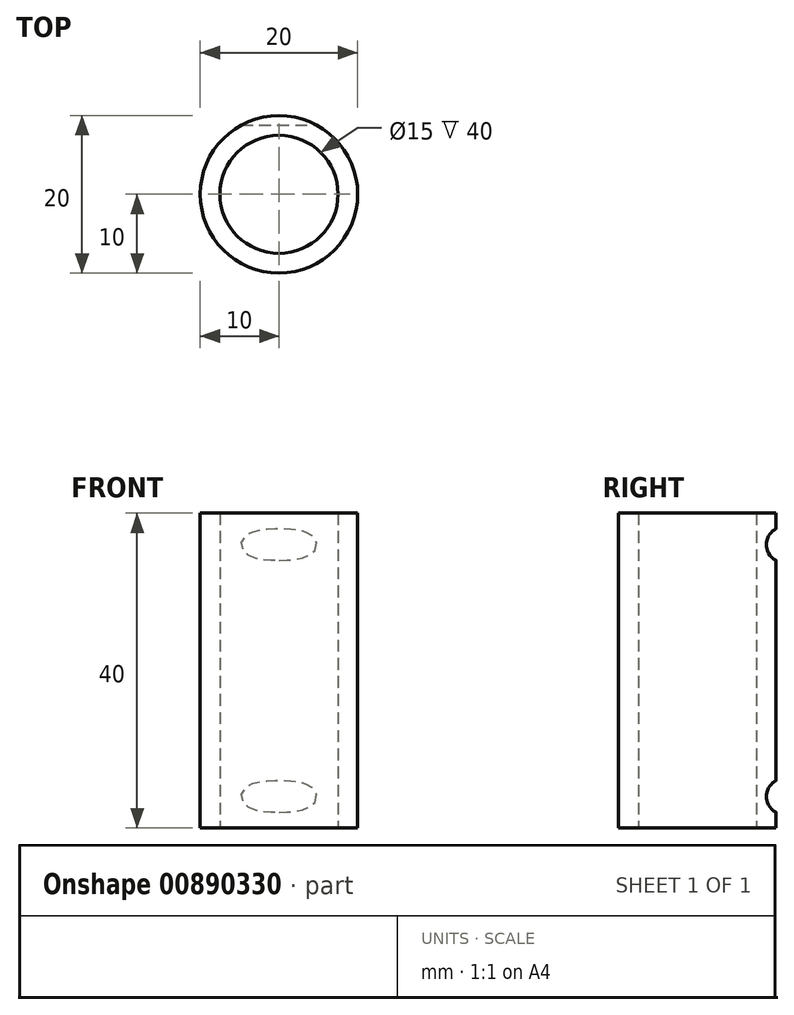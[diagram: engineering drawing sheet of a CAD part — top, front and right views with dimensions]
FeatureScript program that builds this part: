
annotation { "Feature Type Name" : "Feature", "Feature Type Description" : "" }
export const myFeature = defineFeature(function(context is Context, id is Id, definition is map)
    precondition{}
    {
        {
            var Q0;
            Q0=qCreatedBy(makeId("Top.planeOp"),FACE);
            var sketch = newSketch(context, id + "F0", { "sketchPlane" : qUnion([Q0])});
            skCircle(sketch, "E0", {"center": v(0, 0) * mm, "radius": 7.5 * mm});
            skCircle(sketch, "E1", {"center": v(0, 0) * mm, "radius": 10 * mm});
            skSolve(sketch);
        }
        {
            var Q0;
            Q0 = qSketchRegion(id + "F0", true);
            extrude(context, id + "F1", {"entities" : qUnion([Q0]), "depth" : 20 * mm, "offsetDistance" : 25 * mm, "hasSecondDirection" : true, "secondDirectionOppositeDirection" : true, "secondDirectionDepth" : 20 * mm});
        }
        {
            var Q0;
            Q0=qCreatedBy(makeId("Right.planeOp"),FACE);
            cPlane(context, id + "F2", {"entities" : qUnion([Q0]), "cplaneType" : CPlaneType.OFFSET, "offset" : 20 * mm, "width" : 150 * mm, "height" : 150 * mm});
        }
        {
            var Q0;
            Q0=qCreatedBy(id+"F2.planeOp",FACE);
            var sketch = newSketch(context, id + "F3", { "sketchPlane" : qUnion([Q0])});
            skLineSegment(sketch, "E2", {"start": v(0, 0) * mm, "end": v(10, 0) * mm, "construction": true});
            skLineSegment(sketch, "E3", {"start": v(10, 0) * mm, "end": v(10, 16) * mm, "construction": true});
            skLineSegment(sketch, "E4", {"start": v(10, 16) * mm, "end": v(10, 14) * mm});
            skLineSegment(sketch, "E5", {"start": v(10, 16) * mm, "end": v(10, 18) * mm});
            skArc(sketch, "E6", {"start": v(10, 18) * mm, "mid": v(8.76, 16) * mm, "end": v(10, 14) * mm});
            skArc(sketch, "E7.MirrorCS", {"start": v(10, -18) * mm, "mid": v(8.76, -16) * mm, "end": v(10, -14) * mm});
            skLineSegment(sketch, "E8.MirrorCS", {"start": v(10, -16) * mm, "end": v(10, -18) * mm});
            skLineSegment(sketch, "E9", {"start": v(10, -16) * mm, "end": v(10, -14) * mm});
            skSolve(sketch);
        }
        {
            var Q0;
            Q0 = qSketchRegion(id + "F3", true);
            extrude(context, id + "F4", {"entities" : qUnion([Q0]), "operationType" : NewBodyOperationType.REMOVE, "oppositeDirection" : true, "depth" : 50 * mm, "offsetDistance" : 25 * mm});
        }
    });
